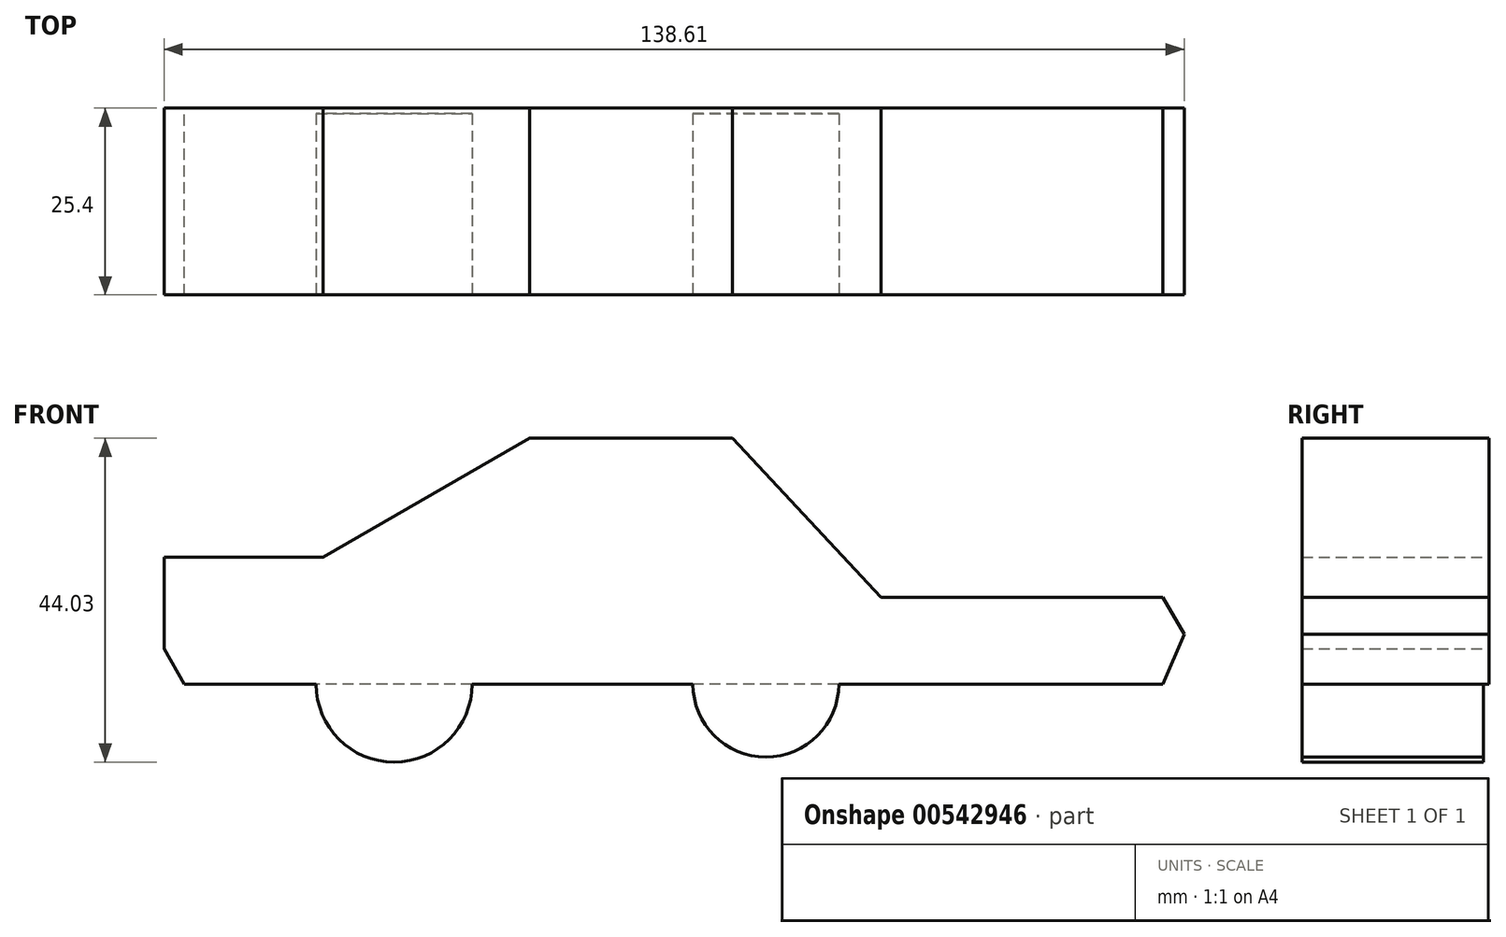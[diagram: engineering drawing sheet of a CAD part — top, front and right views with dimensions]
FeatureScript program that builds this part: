
annotation { "Feature Type Name" : "Feature", "Feature Type Description" : "" }
export const myFeature = defineFeature(function(context is Context, id is Id, definition is map)
    precondition{}
    {
        {
            var Q0;
            Q0=qCreatedBy(makeId("Front.planeOp"),FACE);
            var sketch = newSketch(context, id + "F0", { "sketchPlane" : qUnion([Q0])});
            skLineSegment(sketch, "E0", {"start": v(-77.23, 0) * mm, "end": v(-55.66, 0) * mm});
            skLineSegment(sketch, "E1", {"start": v(-55.66, 0) * mm, "end": v(-27.55, 16.14) * mm});
            skLineSegment(sketch, "E2", {"start": v(-27.55, 16.14) * mm, "end": v(0, 16.14) * mm});
            skLineSegment(sketch, "E3", {"start": v(0, 16.14) * mm, "end": v(20.2, -5.48) * mm});
            skLineSegment(sketch, "E4", {"start": v(20.2, -5.48) * mm, "end": v(58.48, -5.48) * mm});
            skLineSegment(sketch, "E5", {"start": v(58.48, -5.48) * mm, "end": v(61.38, -10.53) * mm});
            skLineSegment(sketch, "E6", {"start": v(61.38, -10.53) * mm, "end": v(58.48, -17.28) * mm});
            skLineSegment(sketch, "E7", {"start": v(58.48, -17.28) * mm, "end": v(-74.47, -17.28) * mm});
            skLineSegment(sketch, "E8", {"start": v(-74.47, -17.28) * mm, "end": v(-77.23, -12.48) * mm});
            skLineSegment(sketch, "E9", {"start": v(-77.23, -12.48) * mm, "end": v(-77.23, 0) * mm});
            skSolve(sketch);
        }
        {
            var Q0;
            Q0=makeQuery(id+"F0.imprint","IMPRINT",FACE,{"disambiguationData":[TD([[makeQuery(id+"F0.imprint","IMPRINT",EDGE,{"derivedFrom":sQuery(id+"F0.wireOp",EDGE,"E0")}),-1.0]])]});
            extrude(context, id + "F1", {"entities" : qUnion([Q0]), "depth" : 25.4 * mm, "offsetDistance" : 25.4 * mm});
        }
        {
            var Q0;
            Q0=makeQuery(id+"F1.opExtrude","CAP_FACE",FACE,{"disambiguationData":[OSD([sQuery(id+"F0.wireOp",EDGE,"E0"),sQuery(id+"F0.wireOp",EDGE,"E1"),sQuery(id+"F0.wireOp",EDGE,"E2"),sQuery(id+"F0.wireOp",EDGE,"E3"),sQuery(id+"F0.wireOp",EDGE,"E4"),sQuery(id+"F0.wireOp",EDGE,"E5"),sQuery(id+"F0.wireOp",EDGE,"E6"),sQuery(id+"F0.wireOp",EDGE,"E7"),sQuery(id+"F0.wireOp",EDGE,"E8"),sQuery(id+"F0.wireOp",EDGE,"E9")])],"isStart":false});
            var sketch = newSketch(context, id + "F2", { "sketchPlane" : qUnion([Q0])});
            skCircle(sketch, "E10", {"center": v(-45.98, -17.28) * mm, "radius": 10.6 * mm});
            skCircle(sketch, "E11", {"center": v(4.54, -17.28) * mm, "radius": 9.92 * mm});
            skSolve(sketch);
        }
        {
            var Q0;
            {var subQ0=sQuery(id+"F2.wireOp",EDGE,"E10");var subQ1=makeQuery(id+"F1.opExtrude","CAP_EDGE",EDGE,{"disambiguationData":[OSD([sQuery(id+"F0.wireOp",EDGE,"E7")])],"isStart":false});var subQ2=makeQuery(id+"F2.imprint","INTERSECT",VERTEX,{"disambiguationData":[OD(0.0)],"derivedFrom":[subQ1,subQ0]});Q0=makeQuery(id+"F2.imprint","IMPRINT",FACE,{"disambiguationData":[TD([[makeQuery(id+"F2.imprint","IMPRINT",EDGE,{"disambiguationData":[TD([[subQ2,1.0]])],"derivedFrom":subQ0}),1.0]])]});}
            var Q1;
            {var subQ0=sQuery(id+"F2.wireOp",EDGE,"E10");var subQ1=makeQuery(id+"F1.opExtrude","CAP_EDGE",EDGE,{"disambiguationData":[OSD([sQuery(id+"F0.wireOp",EDGE,"E7")])],"isStart":false});var subQ2=makeQuery(id+"F2.imprint","INTERSECT",VERTEX,{"disambiguationData":[OD(0.0)],"derivedFrom":[subQ1,subQ0]});Q1=makeQuery(id+"F2.imprint","IMPRINT",FACE,{"disambiguationData":[TD([[makeQuery(id+"F2.imprint","IMPRINT",EDGE,{"disambiguationData":[TD([[subQ2,-1.0]])],"derivedFrom":subQ0}),1.0]])]});}
            var Q2;
            {var subQ0=sQuery(id+"F2.wireOp",EDGE,"E11");var subQ1=makeQuery(id+"F1.opExtrude","CAP_EDGE",EDGE,{"disambiguationData":[OSD([sQuery(id+"F0.wireOp",EDGE,"E7")])],"isStart":false});var subQ2=makeQuery(id+"F2.imprint","INTERSECT",VERTEX,{"disambiguationData":[OD(0.0)],"derivedFrom":[subQ1,subQ0]});Q2=makeQuery(id+"F2.imprint","IMPRINT",FACE,{"disambiguationData":[TD([[makeQuery(id+"F2.imprint","IMPRINT",EDGE,{"disambiguationData":[TD([[subQ2,1.0]])],"derivedFrom":subQ0}),1.0]])]});}
            var Q3;
            {var subQ0=sQuery(id+"F2.wireOp",EDGE,"E11");var subQ1=makeQuery(id+"F1.opExtrude","CAP_EDGE",EDGE,{"disambiguationData":[OSD([sQuery(id+"F0.wireOp",EDGE,"E7")])],"isStart":false});var subQ2=makeQuery(id+"F2.imprint","INTERSECT",VERTEX,{"disambiguationData":[OD(0.0)],"derivedFrom":[subQ1,subQ0]});Q3=makeQuery(id+"F2.imprint","IMPRINT",FACE,{"disambiguationData":[TD([[makeQuery(id+"F2.imprint","IMPRINT",EDGE,{"disambiguationData":[TD([[subQ2,-1.0]])],"derivedFrom":subQ0}),1.0]])]});}
            extrude(context, id + "F3", {"entities" : qUnion([Q0, Q1, Q2, Q3]), "operationType" : NewBodyOperationType.ADD, "oppositeDirection" : true, "depth" : 24.64 * mm, "offsetDistance" : 25.4 * mm});
        }
    });
